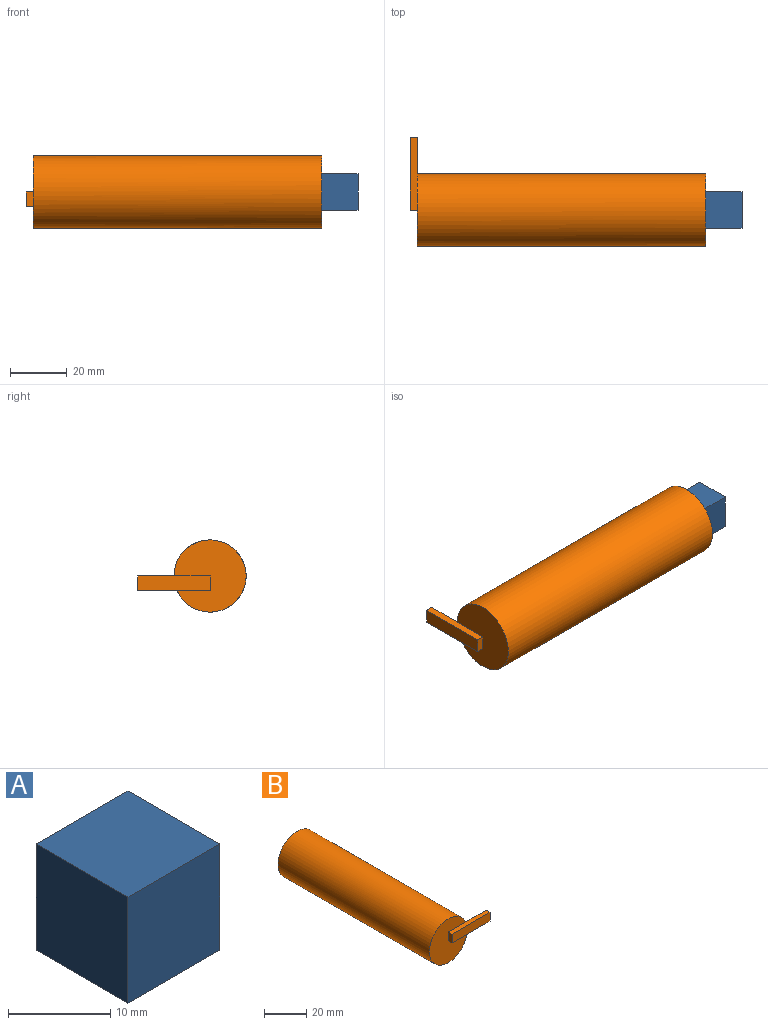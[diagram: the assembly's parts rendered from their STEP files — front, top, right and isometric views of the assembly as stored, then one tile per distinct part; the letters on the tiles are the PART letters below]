
ASSEMBLY  parts=2 mates=1
PART A: 6 faces, bbox 12.7x12.7x12.7 mm
  f0: plane 12.7x12.7mm, normal (0,0,-1), area 161.3mm2, adj f1,f3,f4,f5
  f1: plane 12.7x12.7mm, normal (1,0,0), area 161.3mm2, adj f0,f2,f4,f5
  f2: plane 12.7x12.7mm, normal (0,0,1), area 161.3mm2, adj f1,f3,f4,f5
  f3: plane 12.7x12.7mm, normal (-1,0,0), area 161.3mm2, adj f0,f2,f4,f5
  f4: plane 12.7x12.7mm, normal (0,-1,0), area 161.3mm2, adj f0,f1,f2,f3
  f5: plane 12.7x12.7mm, normal (0,1,0), area 161.3mm2, adj f0,f1,f2,f3
PART B: 9 faces, bbox 38.1x104.1x25.4 mm
  f0: plane 25.4x25.4mm, normal (0,-1,0), area 444mm2, adj f1,f4,f5,f6
  f1: cylinder r=12.7mm len=101.6mm, axis (0,1,0), area 8107.3mm2, adj f0,f2,f3
  f2: plane 25.4x25.4mm, normal (0,1,0), area 506.7mm2, adj f1
  f3: plane 13.76x5.08mm, normal (0,1,0), area 66.3mm2, adj f1,f4,f6,f7
  f4: plane 25.4x2.54mm, normal (0,0,1), area 64.5mm2, adj f0,f3,f5,f7,f8
  f5: plane 5.08x2.54mm, normal (-1,0,0), area 12.9mm2, adj f0,f4,f6,f8
  f6: plane 25.4x2.54mm, normal (0,0,-1), area 64.5mm2, adj f0,f3,f5,f7,f8
  f7: plane 5.08x2.54mm, normal (1,0,0), area 12.9mm2, adj f3,f4,f6,f8
  f8: plane 25.4x5.08mm, normal (0,-1,0), area 129mm2, adj f4,f5,f6,f7
PLACE A t=(-9.45,51.85,-42.75)mm
PLACE B rot(axis=(-0.71,-0.71,0),180deg) t=(-15.8,45.5,-14.17)mm
MATE slider A.f3 <-> B.f1  axis (-1,0,0) through (-15.8,45.5,-14.17)mm
